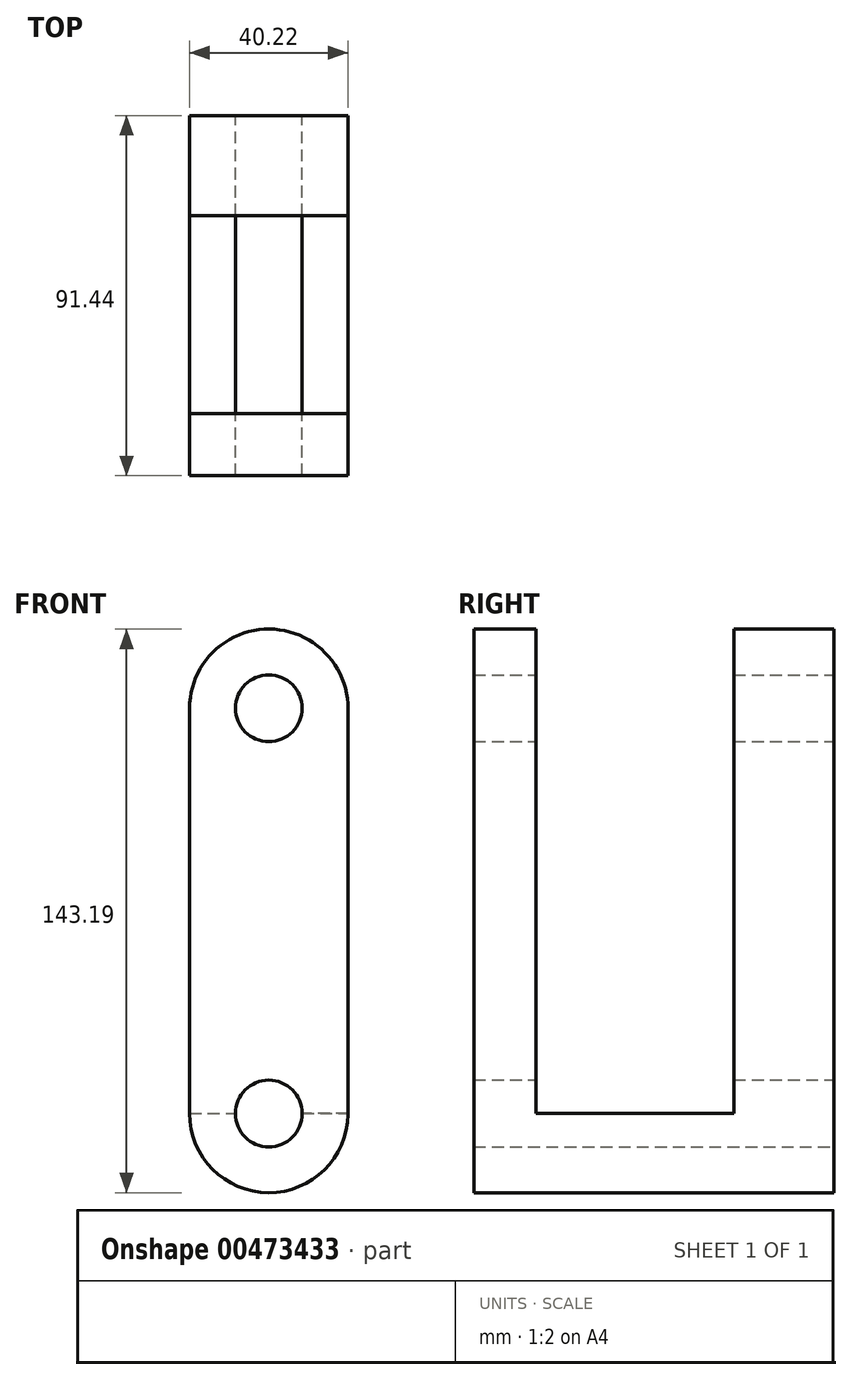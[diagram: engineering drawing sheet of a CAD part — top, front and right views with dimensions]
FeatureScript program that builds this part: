
annotation { "Feature Type Name" : "Feature", "Feature Type Description" : "" }
export const myFeature = defineFeature(function(context is Context, id is Id, definition is map)
    precondition{}
    {
        {
            var Q0;
            Q0=qCreatedBy(makeId("Front.planeOp"),FACE);
            var sketch = newSketch(context, id + "F0", { "sketchPlane" : qUnion([Q0])});
            skArc(sketch, "E0", {"start": v(20.1, 54.42) * mm, "mid": v(0.1, 74.72) * mm, "end": v(-20.11, 54.61) * mm});
            skCircle(sketch, "E1", {"center": v(0, -48.36) * mm, "radius": 20.11 * mm});
            skLineSegment(sketch, "E2.left", {"start": v(-20.11, 54.61) * mm, "end": v(-20.11, -48.55) * mm});
            skLineSegment(sketch, "E2.right", {"start": v(20.1, 54.61) * mm, "end": v(20.1, -48.55) * mm});
            skCircle(sketch, "E3", {"center": v(0, 54.61) * mm, "radius": 8.48 * mm});
            skCircle(sketch, "E4", {"center": v(0, -48.36) * mm, "radius": 8.48 * mm});
            skSolve(sketch);
        }
        {
            var Q0;
            {var subQ1=sQuery(id+"F0.wireOp",EDGE,"E0");Q0=makeQuery(id+"F0.imprint","IMPRINT",FACE,{"disambiguationData":[TD([[makeQuery(id+"F0.imprint","IMPRINT",EDGE,{"derivedFrom":subQ1}),1.0]])]});}
            var Q1;
            Q1=makeQuery(id+"F0.imprint","IMPRINT",FACE,{"disambiguationData":[TD([[makeQuery(id+"F0.imprint","IMPRINT",EDGE,{"derivedFrom":sQuery(id+"F0.wireOp",EDGE,"E4")}),-1.0]])]});
            extrude(context, id + "F1", {"entities" : qUnion([Q0, Q1]), "depth" : 91.44 * mm});
        }
        {
            var Q0;
            Q0=makeQuery(id+"F1.opExtrude","SWEPT_FACE",FACE,{"disambiguationData":[OSD([sQuery(id+"F0.wireOp",EDGE,"E2.left")])]});
            var sketch = newSketch(context, id + "F2", { "sketchPlane" : qUnion([Q0])});
            skLineSegment(sketch, "E5.bottom", {"start": v(75.64, -48.36) * mm, "end": v(15.8, -48.36) * mm});
            skLineSegment(sketch, "E5.top", {"start": v(75.64, 157.58) * mm, "end": v(15.8, 157.58) * mm});
            skLineSegment(sketch, "E5.left", {"start": v(75.64, -48.36) * mm, "end": v(75.64, 157.58) * mm});
            skLineSegment(sketch, "E5.right", {"start": v(15.8, -48.36) * mm, "end": v(15.8, 157.58) * mm});
            skPoint(sketch, "E5.middle", {"position": v(45.72, 54.61) * mm});
            skSolve(sketch);
        }
        {
            var Q0;
            {var subQ0=sQuery(id+"F2.wireOp",EDGE,"E5.top");Q0=makeQuery(id+"F2.imprint","IMPRINT",FACE,{"disambiguationData":[TD([[makeQuery(id+"F2.imprint","IMPRINT",EDGE,{"derivedFrom":subQ0}),1.0]])]});}
            var Q1;
            {var subQ0=sQuery(id+"F2.wireOp",EDGE,"E5.bottom");Q1=makeQuery(id+"F2.imprint","IMPRINT",FACE,{"disambiguationData":[TD([[makeQuery(id+"F2.imprint","IMPRINT",EDGE,{"derivedFrom":subQ0}),-1.0]])]});}
            extrude(context, id + "F3", {"entities" : qUnion([Q0, Q1]), "operationType" : NewBodyOperationType.REMOVE, "oppositeDirection" : true, "depth" : 57.66 * mm});
        }
        {
            var Q0;
            Q0 = qSketchRegion(id + "F0", true);
            extrude(context, id + "F4", {"entities" : qUnion([Q0]), "operationType" : NewBodyOperationType.ADD, "depth" : 25.4 * mm});
        }
        {
            var Q0;
            Q0=sQuery(id+"F0.wireOp",EDGE,"E1");
            extrude(context, id + "F5", {"bodyType" : ToolBodyType.SURFACE, "surfaceEntities" : qUnion([Q0]), "depth" : 91.44 * mm});
        }
    });
